# Revit family: R586RFL_151-163
name_source: partatom
category: Pipe Accessories
units: mm (PartAtom-declared; Revit-internal decimal feet)

## family parameters
Always vertical = No
Cut with Voids When Loaded = No
Part Type = Normal
Round Connector Dimension = Use Diameter
Shared = No
Work Plane-Based = No

## types (4) — shared parameters
Description = Gruppi premontati di distribuzione/regolazione, attacchi flangiati
Manufacturer = Giacomini
Maximum Working Temperature = -273 °C
Mixing Diverting Valve Insulation = Yes
Nominal Diameter = 40 mm  [stored 0.131234 ft]
Series = R586RFL
zero-valued in all types: Default Elevation

## per-type parameters (varying)
| type | 63-53 | Punp visibility |
| R586RY151 | No | Yes |
| R586RY153 | Yes | Yes |
| R586RY161 | No | No |
| R586RY163 | Yes | No |

note: column(s) folded — value = type name in every type: Code, Model

note: [stored X ft] marks values corroborated as IEEE doubles in the binary element streams (Revit-internal decimal feet)

## geometry (parser evidence)
native form markers: Sweep x6
no freeform markers — native parametric forms only
